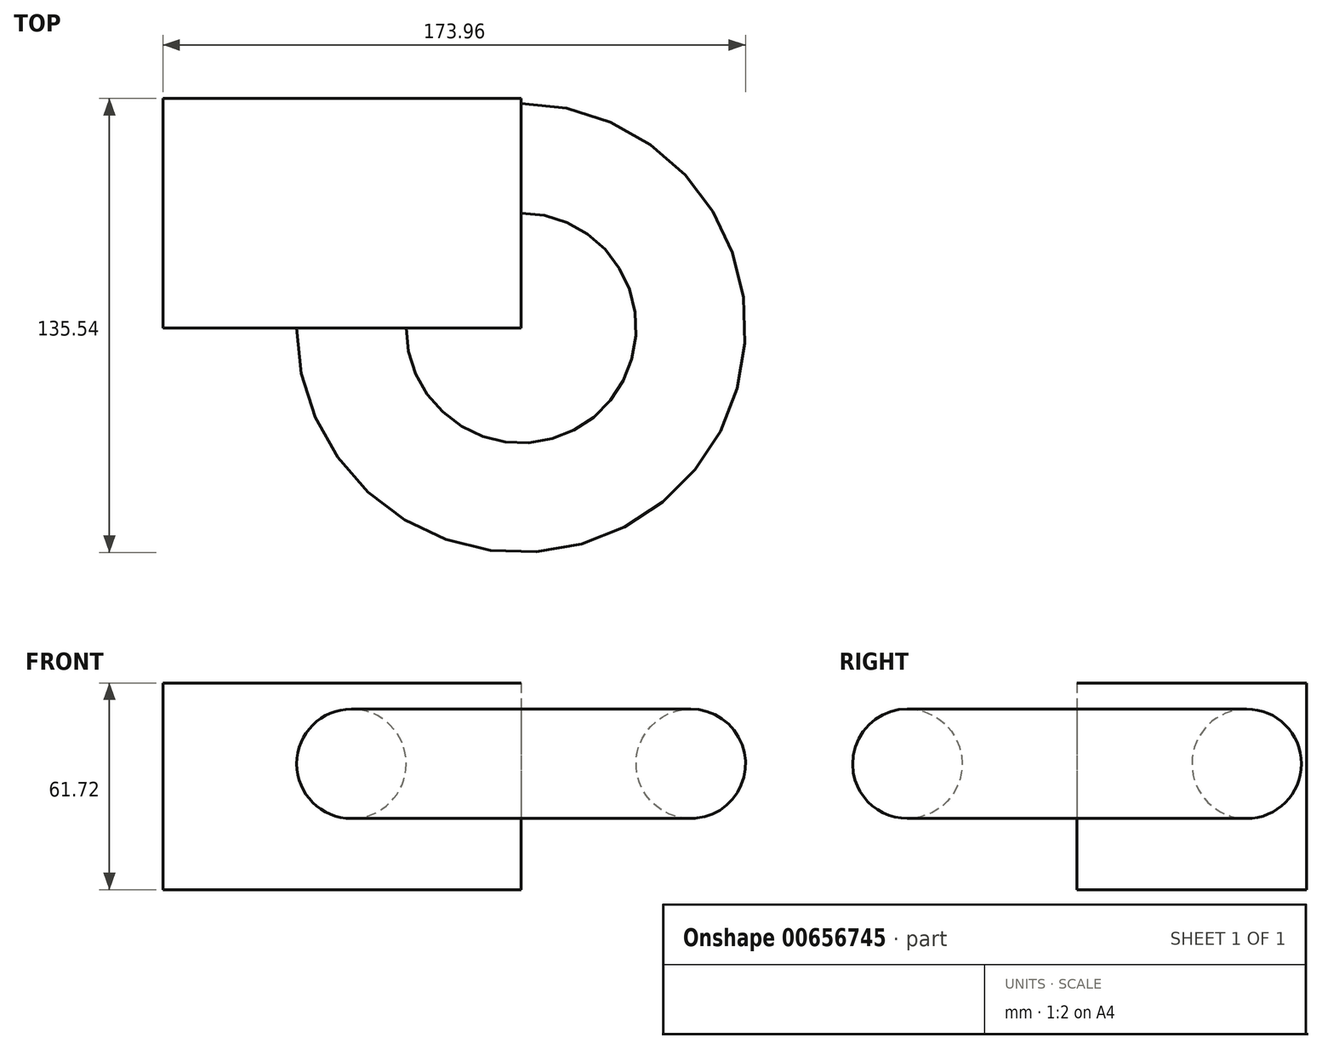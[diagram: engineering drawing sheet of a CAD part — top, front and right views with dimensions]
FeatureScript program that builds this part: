
annotation { "Feature Type Name" : "Feature", "Feature Type Description" : "" }
export const myFeature = defineFeature(function(context is Context, id is Id, definition is map)
    precondition{}
    {
        {
            var Q0;
            Q0=qCreatedBy(makeId("Top.planeOp"),FACE);
            var sketch = newSketch(context, id + "F0", { "sketchPlane" : qUnion([Q0])});
            skLineSegment(sketch, "E0.bottom", {"start": v(-50.75, -20.08) * mm, "end": v(56.2, -20.08) * mm});
            skLineSegment(sketch, "E0.top", {"start": v(-50.75, 48.45) * mm, "end": v(56.2, 48.45) * mm});
            skLineSegment(sketch, "E0.left", {"start": v(-50.75, -20.08) * mm, "end": v(-50.75, 48.45) * mm});
            skLineSegment(sketch, "E0.right", {"start": v(56.2, -20.08) * mm, "end": v(56.2, 48.45) * mm});
            skSolve(sketch);
        }
        {
            var Q0;
            Q0=makeQuery(id+"F0.imprint","IMPRINT",FACE,{"disambiguationData":[TD([[makeQuery(id+"F0.imprint","IMPRINT",EDGE,{"derivedFrom":sQuery(id+"F0.wireOp",EDGE,"E0.bottom")}),1.0]])]});
            extrude(context, id + "F1", {"entities" : qUnion([Q0]), "depth" : 61.72 * mm, "offsetDistance" : 25.4 * mm});
        }
        {
            var Q0;
            Q0=makeQuery(id+"F1.opExtrude","SWEPT_FACE",FACE,{"disambiguationData":[OSD([sQuery(id+"F0.wireOp",EDGE,"E0.bottom")])]});
            var sketch = newSketch(context, id + "F2", { "sketchPlane" : qUnion([Q0])});
            skCircle(sketch, "E1", {"center": v(5.53, 37.6) * mm, "radius": 16.35 * mm});
            skSolve(sketch);
        }
        {
            var Q0;
            Q0=makeQuery(id+"F2.imprint","IMPRINT",FACE,{"disambiguationData":[TD([[makeQuery(id+"F2.imprint","IMPRINT",EDGE,{"derivedFrom":sQuery(id+"F2.wireOp",EDGE,"E1")}),1.0]])]});
            var Q1;
            Q1=makeQuery(id+"F1.opExtrude","SWEPT_EDGE",EDGE,{"disambiguationData":[OSD([sQuery(id+"F0.wireOp",EDGE,"E0.bottom"),sQuery(id+"F0.wireOp",EDGE,"E0.right")])]});
            revolve(context, id + "F3", {"operationType" : NewBodyOperationType.ADD, "entities" : qUnion([Q0]), "axis" : qUnion([Q1]), "revolveType" : RevolveType.FULL});
        }
    });
